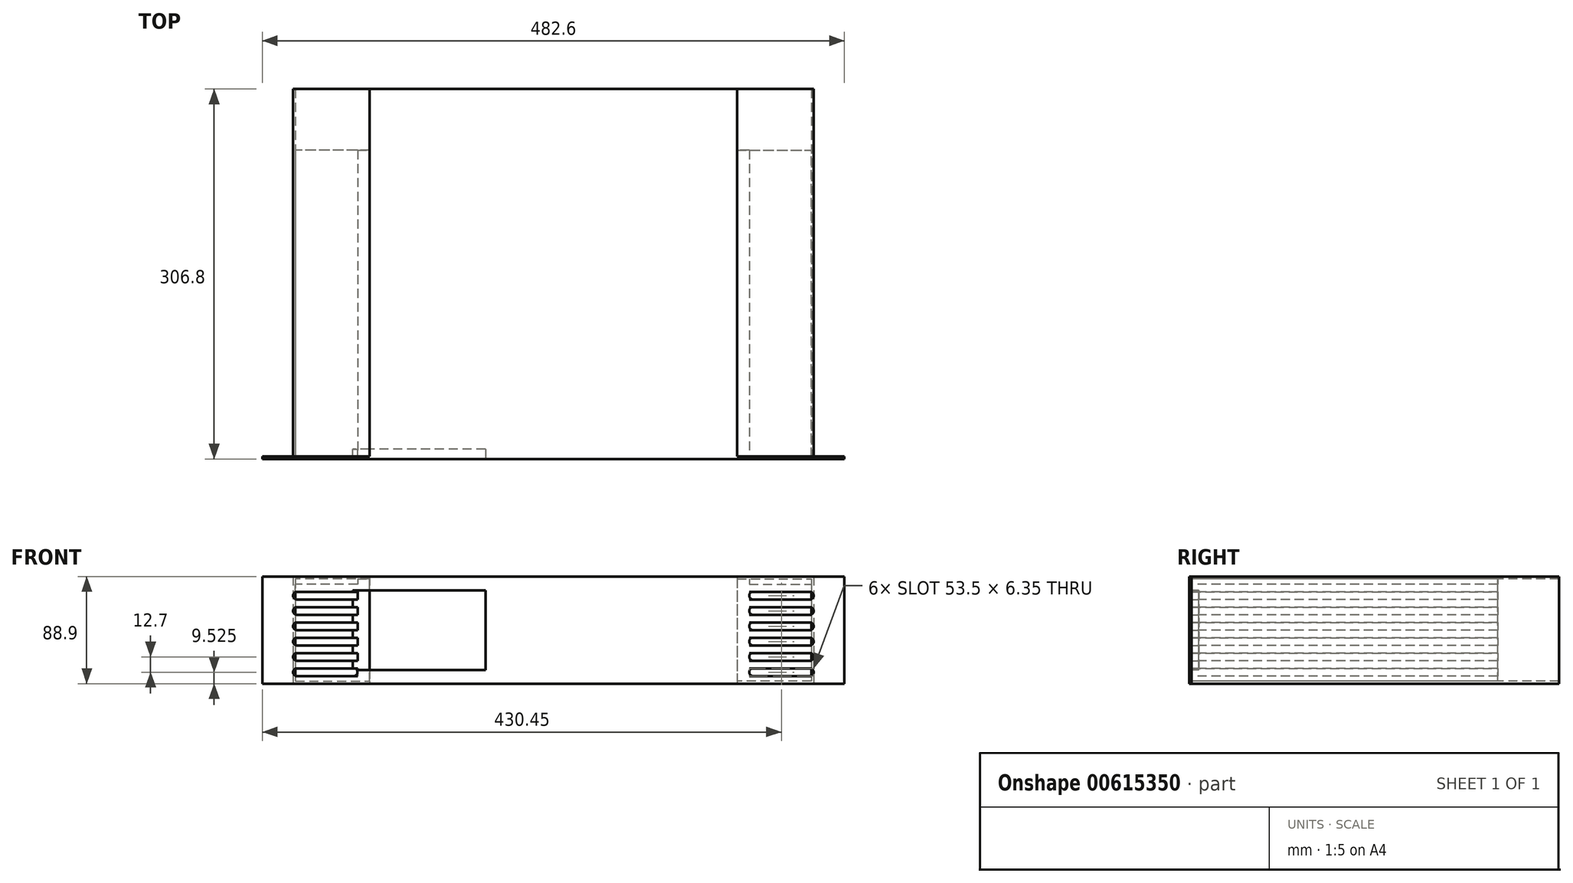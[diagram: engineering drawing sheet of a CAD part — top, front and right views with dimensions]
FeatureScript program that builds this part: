
annotation { "Feature Type Name" : "Feature", "Feature Type Description" : "" }
export const myFeature = defineFeature(function(context is Context, id is Id, definition is map)
    precondition{}
    {
        {
            var Q0;
            Q0=qCreatedBy(makeId("Top.planeOp"),FACE);
            var sketch = newSketch(context, id + "F0", { "sketchPlane" : qUnion([Q0])});
            skLineSegment(sketch, "E0.bottom", {"start": v(152.4, -152.4) * mm, "end": v(-152.4, -152.4) * mm});
            skLineSegment(sketch, "E0.top", {"start": v(152.4, 152.4) * mm, "end": v(-152.4, 152.4) * mm});
            skLineSegment(sketch, "E0.left", {"start": v(152.4, -152.4) * mm, "end": v(152.4, 152.4) * mm});
            skLineSegment(sketch, "E0.right", {"start": v(-152.4, -152.4) * mm, "end": v(-152.4, 152.4) * mm});
            skPoint(sketch, "E0.middle", {"position": v(0, 0) * mm});
            skSolve(sketch);
        }
        {
            var Q0;
            Q0=makeQuery(id+"F0.imprint","IMPRINT",FACE,{"disambiguationData":[TD([[makeQuery(id+"F0.imprint","IMPRINT",EDGE,{"derivedFrom":sQuery(id+"F0.wireOp",EDGE,"E0.bottom")}),-1.0]])]});
            extrude(context, id + "F1", {"entities" : qUnion([Q0]), "depth" : 88.9 * mm, "offsetDistance" : 25 * mm});
        }
        {
            var Q0;
            Q0=makeQuery(id+"F1.opExtrude","SWEPT_FACE",FACE,{"disambiguationData":[OSD([sQuery(id+"F0.wireOp",EDGE,"E0.bottom")])]});
            var sketch = newSketch(context, id + "F2", { "sketchPlane" : qUnion([Q0])});
            skLineSegment(sketch, "E1.bottom", {"start": v(-241.3, 0) * mm, "end": v(241.3, 0) * mm});
            skLineSegment(sketch, "E1.top", {"start": v(-241.3, 88.9) * mm, "end": v(241.3, 88.9) * mm});
            skLineSegment(sketch, "E1.left", {"start": v(-241.3, 0) * mm, "end": v(-241.3, 88.9) * mm});
            skLineSegment(sketch, "E1.right", {"start": v(241.3, 0) * mm, "end": v(241.3, 88.9) * mm});
            skPoint(sketch, "E1.middle", {"position": v(0, 44.45) * mm});
            skPoint(sketch, "E1.middle.positionSnap0", {"position": v(152.4, 44.45) * mm});
            skPoint(sketch, "E1.centerSnap0", {"position": v(152.4, 44.45) * mm});
            skSolve(sketch);
        }
        {
            var Q0;
            {var subQ2=sQuery(id+"F2.wireOp",EDGE,"E1.left");Q0=makeQuery(id+"F2.imprint","IMPRINT",FACE,{"disambiguationData":[TD([[makeQuery(id+"F2.imprint","IMPRINT",EDGE,{"derivedFrom":subQ2}),-1.0]])]});}
            var Q1;
            {var subQ2=sQuery(id+"F2.wireOp",EDGE,"E1.right");Q1=makeQuery(id+"F2.imprint","IMPRINT",FACE,{"disambiguationData":[TD([[makeQuery(id+"F2.imprint","IMPRINT",EDGE,{"derivedFrom":subQ2}),1.0]])]});}
            var Q2;
            {var subQ1=sQuery(id+"F0.wireOp",EDGE,"E0.bottom");var subQ2=makeQuery(id+"F1.opExtrude","SWEPT_EDGE",EDGE,{"disambiguationData":[OSD([subQ1,sQuery(id+"F0.wireOp",EDGE,"E0.left")])]});Q2=makeQuery(id+"F2.imprint","IMPRINT",FACE,{"disambiguationData":[TD([[makeQuery(id+"F2.imprint","IMPRINT",EDGE,{"derivedFrom":subQ2}),-1.0]])]});}
            extrude(context, id + "F3", {"entities" : qUnion([Q0, Q1, Q2]), "operationType" : NewBodyOperationType.ADD, "depth" : 2 * mm, "offsetDistance" : 25 * mm});
        }
        {
            var Q0;
            {var subQ0=sQuery(id+"F2.wireOp",EDGE,"E1.bottom");var subQ2=sQuery(id+"F0.wireOp",EDGE,"E0.left");var subQ5=sQuery(id+"F2.wireOp",EDGE,"E1.top");var subQ6=sQuery(id+"F2.wireOp",EDGE,"E1.right");Q0=makeQuery(id+"F3.boolean.opBoolean","SPLIT",FACE,{"disambiguationData":[TD([makeQuery(id+"F1.opExtrude","SWEPT_FACE",FACE,{"disambiguationData":[OSD([subQ2])]})])],"derivedFrom":makeQuery(id+"F3.opExtrude","CAP_FACE",FACE,{"disambiguationData":[OSD([subQ0,subQ5,sQuery(id+"F2.wireOp",EDGE,"E1.left"),subQ6])],"isStart":true})});}
            var sketch = newSketch(context, id + "F4", { "sketchPlane" : qUnion([Q0])});
            skLineSegment(sketch, "E2", {"start": v(-152.4, 88.9) * mm, "end": v(-162.4, 88.9) * mm});
            skLineSegment(sketch, "E3", {"start": v(-162.4, 88.9) * mm, "end": v(-162.4, 82.55) * mm});
            skLineSegment(sketch, "E4", {"start": v(-162.4, 82.55) * mm, "end": v(-215.9, 82.55) * mm});
            skLineSegment(sketch, "E5", {"start": v(-215.9, 82.55) * mm, "end": v(-215.9, 76.2) * mm});
            skLineSegment(sketch, "E6", {"start": v(-215.9, 76.2) * mm, "end": v(-162.4, 76.2) * mm});
            skLineSegment(sketch, "E7.0.1.1", {"start": v(-215.9, 69.85) * mm, "end": v(-215.9, 63.5) * mm});
            skLineSegment(sketch, "E7.0.1.2", {"start": v(-162.4, 69.85) * mm, "end": v(-215.9, 69.85) * mm});
            skLineSegment(sketch, "E7.0.1.3", {"start": v(-215.9, 63.5) * mm, "end": v(-162.4, 63.5) * mm});
            skLineSegment(sketch, "E7.0.1.4", {"start": v(-162.4, 76.2) * mm, "end": v(-162.4, 69.85) * mm});
            skLineSegment(sketch, "E7.0.2.1", {"start": v(-215.9, 57.15) * mm, "end": v(-215.9, 50.8) * mm});
            skLineSegment(sketch, "E7.0.2.2", {"start": v(-162.4, 57.15) * mm, "end": v(-215.9, 57.15) * mm});
            skLineSegment(sketch, "E7.0.2.3", {"start": v(-215.9, 50.8) * mm, "end": v(-162.4, 50.8) * mm});
            skLineSegment(sketch, "E7.0.2.4", {"start": v(-162.4, 63.5) * mm, "end": v(-162.4, 57.15) * mm});
            skLineSegment(sketch, "E7.0.3.1", {"start": v(-215.9, 44.45) * mm, "end": v(-215.9, 38.1) * mm});
            skLineSegment(sketch, "E7.0.3.2", {"start": v(-162.4, 44.45) * mm, "end": v(-215.9, 44.45) * mm});
            skLineSegment(sketch, "E7.0.3.3", {"start": v(-215.9, 38.1) * mm, "end": v(-162.4, 38.1) * mm});
            skLineSegment(sketch, "E7.0.3.4", {"start": v(-162.4, 50.8) * mm, "end": v(-162.4, 44.45) * mm});
            skLineSegment(sketch, "E7.0.4.1", {"start": v(-215.9, 31.75) * mm, "end": v(-215.9, 25.4) * mm});
            skLineSegment(sketch, "E7.0.4.2", {"start": v(-162.4, 31.75) * mm, "end": v(-215.9, 31.75) * mm});
            skLineSegment(sketch, "E7.0.4.3", {"start": v(-215.9, 25.4) * mm, "end": v(-162.4, 25.4) * mm});
            skLineSegment(sketch, "E7.0.4.4", {"start": v(-162.4, 38.1) * mm, "end": v(-162.4, 31.75) * mm});
            skLineSegment(sketch, "E7.0.5.1", {"start": v(-215.9, 19.05) * mm, "end": v(-215.9, 12.7) * mm});
            skLineSegment(sketch, "E7.0.5.2", {"start": v(-162.4, 19.05) * mm, "end": v(-215.9, 19.05) * mm});
            skLineSegment(sketch, "E7.0.5.3", {"start": v(-215.9, 12.7) * mm, "end": v(-162.4, 12.7) * mm});
            skLineSegment(sketch, "E7.0.5.4", {"start": v(-162.4, 25.4) * mm, "end": v(-162.4, 19.05) * mm});
            skLineSegment(sketch, "E7.0.6.1", {"start": v(-215.9, 6.35) * mm, "end": v(-215.9, 0) * mm});
            skLineSegment(sketch, "E7.0.6.2", {"start": v(-162.4, 6.35) * mm, "end": v(-215.9, 6.35) * mm});
            skLineSegment(sketch, "E7.0.6.3", {"start": v(-215.9, 0) * mm, "end": v(-162.4, 0) * mm});
            skLineSegment(sketch, "E7.0.6.4", {"start": v(-162.4, 12.7) * mm, "end": v(-162.4, 6.35) * mm});
            skLineSegment(sketch, "E7.direction1", {"start": v(-215.9, 76.2) * mm, "end": v(-190.9, 76.2) * mm, "construction": true});
            skLineSegment(sketch, "E7.direction2", {"start": v(-215.9, 76.2) * mm, "end": v(-215.9, 63.5) * mm, "construction": true});
            skLineSegment(sketch, "E8", {"start": v(-162.4, 0) * mm, "end": v(-152.4, 0) * mm});
            skLineSegment(sketch, "E9", {"start": v(-152.4, 0) * mm, "end": v(-152.4, 88.9) * mm});
            skLineSegment(sketch, "E10.MirrorCS", {"start": v(215.9, 69.85) * mm, "end": v(215.9, 63.5) * mm});
            skLineSegment(sketch, "E11.MirrorCS", {"start": v(162.4, 19.05) * mm, "end": v(215.9, 19.05) * mm});
            skLineSegment(sketch, "E12.MirrorCS", {"start": v(162.4, 25.4) * mm, "end": v(162.4, 19.05) * mm});
            skLineSegment(sketch, "E13.MirrorCS", {"start": v(215.9, 57.15) * mm, "end": v(215.9, 50.8) * mm});
            skLineSegment(sketch, "E14.MirrorCS", {"start": v(162.4, 69.85) * mm, "end": v(215.9, 69.85) * mm});
            skLineSegment(sketch, "E15.MirrorCS", {"start": v(215.9, 12.7) * mm, "end": v(162.4, 12.7) * mm});
            skLineSegment(sketch, "E16.MirrorCS", {"start": v(162.4, 88.9) * mm, "end": v(162.4, 82.55) * mm});
            skLineSegment(sketch, "E17.MirrorCS", {"start": v(215.9, 82.55) * mm, "end": v(215.9, 76.2) * mm});
            skLineSegment(sketch, "E18.MirrorCS", {"start": v(152.4, 88.9) * mm, "end": v(162.4, 88.9) * mm});
            skLineSegment(sketch, "E19.MirrorCS", {"start": v(162.4, 82.55) * mm, "end": v(215.9, 82.55) * mm});
            skLineSegment(sketch, "E20.MirrorCS", {"start": v(162.4, 50.8) * mm, "end": v(162.4, 44.45) * mm});
            skLineSegment(sketch, "E21.MirrorCS", {"start": v(215.9, 25.4) * mm, "end": v(162.4, 25.4) * mm});
            skLineSegment(sketch, "E22.MirrorCS", {"start": v(215.9, 44.45) * mm, "end": v(215.9, 38.1) * mm});
            skLineSegment(sketch, "E23.MirrorCS", {"start": v(162.4, 38.1) * mm, "end": v(162.4, 31.75) * mm});
            skLineSegment(sketch, "E24.MirrorCS", {"start": v(162.4, 6.35) * mm, "end": v(215.9, 6.35) * mm});
            skLineSegment(sketch, "E25.MirrorCS", {"start": v(215.9, 6.35) * mm, "end": v(215.9, 0) * mm});
            skLineSegment(sketch, "E26.MirrorCS", {"start": v(215.9, 76.2) * mm, "end": v(215.9, 63.5) * mm, "construction": true});
            skLineSegment(sketch, "E27.MirrorCS", {"start": v(215.9, 76.2) * mm, "end": v(190.9, 76.2) * mm, "construction": true});
            skLineSegment(sketch, "E28.MirrorCS", {"start": v(162.4, 31.75) * mm, "end": v(215.9, 31.75) * mm});
            skLineSegment(sketch, "E29.MirrorCS", {"start": v(152.4, 0) * mm, "end": v(152.4, 88.9) * mm});
            skLineSegment(sketch, "E30.MirrorCS", {"start": v(215.9, 38.1) * mm, "end": v(162.4, 38.1) * mm});
            skLineSegment(sketch, "E31.MirrorCS", {"start": v(162.4, 44.45) * mm, "end": v(215.9, 44.45) * mm});
            skLineSegment(sketch, "E32.MirrorCS", {"start": v(215.9, 76.2) * mm, "end": v(162.4, 76.2) * mm});
            skLineSegment(sketch, "E33.MirrorCS", {"start": v(215.9, 19.05) * mm, "end": v(215.9, 12.7) * mm});
            skLineSegment(sketch, "E34.MirrorCS", {"start": v(215.9, 31.75) * mm, "end": v(215.9, 25.4) * mm});
            skLineSegment(sketch, "E35.MirrorCS", {"start": v(215.9, 63.5) * mm, "end": v(162.4, 63.5) * mm});
            skLineSegment(sketch, "E36.MirrorCS", {"start": v(162.4, 76.2) * mm, "end": v(162.4, 69.85) * mm});
            skLineSegment(sketch, "E37.MirrorCS", {"start": v(215.9, 50.8) * mm, "end": v(162.4, 50.8) * mm});
            skLineSegment(sketch, "E38.MirrorCS", {"start": v(162.4, 57.15) * mm, "end": v(215.9, 57.15) * mm});
            skLineSegment(sketch, "E39.MirrorCS", {"start": v(162.4, 12.7) * mm, "end": v(162.4, 6.35) * mm});
            skLineSegment(sketch, "E40.MirrorCS", {"start": v(162.4, 63.5) * mm, "end": v(162.4, 57.15) * mm});
            skLineSegment(sketch, "E41.MirrorCS", {"start": v(215.9, 0) * mm, "end": v(162.4, 0) * mm});
            skLineSegment(sketch, "E42.MirrorCS", {"start": v(162.4, 0) * mm, "end": v(152.4, 0) * mm});
            skSolve(sketch);
        }
        {
            var Q0;
            Q0=makeQuery(id+"F4.imprint","IMPRINT",FACE,{"disambiguationData":[TD([[makeQuery(id+"F4.imprint","IMPRINT",EDGE,{"derivedFrom":sQuery(id+"F4.wireOp",EDGE,"E2")}),1.0]])]});
            var Q1;
            Q1=makeQuery(id+"F4.imprint","IMPRINT",FACE,{"disambiguationData":[TD([[makeQuery(id+"F4.imprint","IMPRINT",EDGE,{"derivedFrom":sQuery(id+"F4.wireOp",EDGE,"E10.MirrorCS")}),-1.0]])]});
            extrude(context, id + "F5", {"entities" : qUnion([Q0, Q1]), "depth" : 254 * mm, "offsetDistance" : 25 * mm});
        }
        {
            var Q0;
            {var subQ0=sQuery(id+"F2.wireOp",EDGE,"E1.bottom");var subQ2=sQuery(id+"F0.wireOp",EDGE,"E0.left");var subQ5=sQuery(id+"F2.wireOp",EDGE,"E1.top");var subQ6=sQuery(id+"F2.wireOp",EDGE,"E1.right");Q0=makeQuery(id+"F3.boolean.opBoolean","SPLIT",FACE,{"disambiguationData":[TD([makeQuery(id+"F1.opExtrude","SWEPT_FACE",FACE,{"disambiguationData":[OSD([subQ2])]})])],"derivedFrom":makeQuery(id+"F3.opExtrude","CAP_FACE",FACE,{"disambiguationData":[OSD([subQ0,subQ5,sQuery(id+"F2.wireOp",EDGE,"E1.left"),subQ6])],"isStart":true})});}
            var sketch = newSketch(context, id + "F6", { "sketchPlane" : qUnion([Q0])});
            skArc(sketch, "E43", {"start": v(-212.72, 76.2) * mm, "mid": v(-215.9, 73.03) * mm, "end": v(-212.72, 69.85) * mm});
            skArc(sketch, "E44", {"start": v(-165.57, 69.85) * mm, "mid": v(-162.4, 73.03) * mm, "end": v(-165.57, 76.2) * mm});
            skLineSegment(sketch, "E45", {"start": v(-212.72, 69.85) * mm, "end": v(-165.57, 69.85) * mm});
            skLineSegment(sketch, "E46", {"start": v(-212.72, 76.2) * mm, "end": v(-165.57, 76.2) * mm});
            skArc(sketch, "E47.0.1.0", {"start": v(-212.72, 63.5) * mm, "mid": v(-215.9, 60.33) * mm, "end": v(-212.72, 57.15) * mm});
            skLineSegment(sketch, "E47.0.1.1", {"start": v(-212.72, 57.15) * mm, "end": v(-165.57, 57.15) * mm});
            skLineSegment(sketch, "E47.0.1.2", {"start": v(-212.72, 63.5) * mm, "end": v(-165.57, 63.5) * mm});
            skArc(sketch, "E47.0.1.3", {"start": v(-165.57, 57.15) * mm, "mid": v(-162.4, 60.33) * mm, "end": v(-165.57, 63.5) * mm});
            skArc(sketch, "E47.0.2.0", {"start": v(-212.72, 50.8) * mm, "mid": v(-215.9, 47.62) * mm, "end": v(-212.72, 44.45) * mm});
            skLineSegment(sketch, "E47.0.2.1", {"start": v(-212.72, 44.45) * mm, "end": v(-165.57, 44.45) * mm});
            skLineSegment(sketch, "E47.0.2.2", {"start": v(-212.72, 50.8) * mm, "end": v(-165.57, 50.8) * mm});
            skArc(sketch, "E47.0.2.3", {"start": v(-165.57, 44.45) * mm, "mid": v(-162.4, 47.62) * mm, "end": v(-165.57, 50.8) * mm});
            skArc(sketch, "E47.0.3.0", {"start": v(-212.72, 38.1) * mm, "mid": v(-215.9, 34.92) * mm, "end": v(-212.72, 31.75) * mm});
            skLineSegment(sketch, "E47.0.3.1", {"start": v(-212.72, 31.75) * mm, "end": v(-165.57, 31.75) * mm});
            skLineSegment(sketch, "E47.0.3.2", {"start": v(-212.72, 38.1) * mm, "end": v(-165.57, 38.1) * mm});
            skArc(sketch, "E47.0.3.3", {"start": v(-165.57, 31.75) * mm, "mid": v(-162.4, 34.92) * mm, "end": v(-165.57, 38.1) * mm});
            skArc(sketch, "E47.0.4.0", {"start": v(-212.72, 25.4) * mm, "mid": v(-215.9, 22.22) * mm, "end": v(-212.72, 19.05) * mm});
            skLineSegment(sketch, "E47.0.4.1", {"start": v(-212.72, 19.05) * mm, "end": v(-165.57, 19.05) * mm});
            skLineSegment(sketch, "E47.0.4.2", {"start": v(-212.72, 25.4) * mm, "end": v(-165.57, 25.4) * mm});
            skArc(sketch, "E47.0.4.3", {"start": v(-165.57, 19.05) * mm, "mid": v(-162.4, 22.22) * mm, "end": v(-165.57, 25.4) * mm});
            skArc(sketch, "E47.0.5.0", {"start": v(-212.72, 12.7) * mm, "mid": v(-215.9, 9.52) * mm, "end": v(-212.72, 6.35) * mm});
            skLineSegment(sketch, "E47.0.5.1", {"start": v(-212.72, 6.35) * mm, "end": v(-165.57, 6.35) * mm});
            skLineSegment(sketch, "E47.0.5.2", {"start": v(-212.72, 12.7) * mm, "end": v(-165.57, 12.7) * mm});
            skArc(sketch, "E47.0.5.3", {"start": v(-165.57, 6.35) * mm, "mid": v(-162.4, 9.52) * mm, "end": v(-165.57, 12.7) * mm});
            skLineSegment(sketch, "E47.direction1", {"start": v(-212.72, 69.85) * mm, "end": v(-187.72, 69.85) * mm, "construction": true});
            skLineSegment(sketch, "E47.direction2", {"start": v(-212.72, 69.85) * mm, "end": v(-212.72, 57.15) * mm, "construction": true});
            skArc(sketch, "E48.MirrorCS", {"start": v(212.72, 38.1) * mm, "mid": v(215.9, 34.92) * mm, "end": v(212.72, 31.75) * mm});
            skLineSegment(sketch, "E49.MirrorCS", {"start": v(212.72, 6.35) * mm, "end": v(165.57, 6.35) * mm});
            skArc(sketch, "E50.MirrorCS", {"start": v(165.57, 44.45) * mm, "mid": v(162.4, 47.62) * mm, "end": v(165.57, 50.8) * mm});
            skLineSegment(sketch, "E51.MirrorCS", {"start": v(212.72, 50.8) * mm, "end": v(165.57, 50.8) * mm});
            skLineSegment(sketch, "E52.MirrorCS", {"start": v(212.72, 44.45) * mm, "end": v(165.57, 44.45) * mm});
            skArc(sketch, "E53.MirrorCS", {"start": v(212.72, 50.8) * mm, "mid": v(215.9, 47.62) * mm, "end": v(212.72, 44.45) * mm});
            skArc(sketch, "E54.MirrorCS", {"start": v(165.57, 57.15) * mm, "mid": v(162.4, 60.33) * mm, "end": v(165.57, 63.5) * mm});
            skLineSegment(sketch, "E55.MirrorCS", {"start": v(212.72, 69.85) * mm, "end": v(212.72, 57.15) * mm, "construction": true});
            skLineSegment(sketch, "E56.MirrorCS", {"start": v(212.72, 69.85) * mm, "end": v(187.72, 69.85) * mm, "construction": true});
            skLineSegment(sketch, "E57.MirrorCS", {"start": v(212.72, 63.5) * mm, "end": v(165.57, 63.5) * mm});
            skLineSegment(sketch, "E58.MirrorCS", {"start": v(212.72, 57.15) * mm, "end": v(165.57, 57.15) * mm});
            skArc(sketch, "E59.MirrorCS", {"start": v(212.72, 63.5) * mm, "mid": v(215.9, 60.33) * mm, "end": v(212.72, 57.15) * mm});
            skLineSegment(sketch, "E60.MirrorCS", {"start": v(212.72, 76.2) * mm, "end": v(165.57, 76.2) * mm});
            skLineSegment(sketch, "E61.MirrorCS", {"start": v(212.72, 69.85) * mm, "end": v(165.57, 69.85) * mm});
            skLineSegment(sketch, "E62.MirrorCS", {"start": v(212.72, 19.05) * mm, "end": v(165.57, 19.05) * mm});
            skArc(sketch, "E63.MirrorCS", {"start": v(165.57, 69.85) * mm, "mid": v(162.4, 73.03) * mm, "end": v(165.57, 76.2) * mm});
            skArc(sketch, "E64.MirrorCS", {"start": v(212.72, 76.2) * mm, "mid": v(215.9, 73.03) * mm, "end": v(212.72, 69.85) * mm});
            skArc(sketch, "E65.MirrorCS", {"start": v(165.57, 31.75) * mm, "mid": v(162.4, 34.92) * mm, "end": v(165.57, 38.1) * mm});
            skArc(sketch, "E66.MirrorCS", {"start": v(212.72, 25.4) * mm, "mid": v(215.9, 22.22) * mm, "end": v(212.72, 19.05) * mm});
            skLineSegment(sketch, "E67.MirrorCS", {"start": v(212.72, 31.75) * mm, "end": v(165.57, 31.75) * mm});
            skArc(sketch, "E68.MirrorCS", {"start": v(165.57, 19.05) * mm, "mid": v(162.4, 22.22) * mm, "end": v(165.57, 25.4) * mm});
            skLineSegment(sketch, "E69.MirrorCS", {"start": v(212.72, 38.1) * mm, "end": v(165.57, 38.1) * mm});
            skArc(sketch, "E70.MirrorCS", {"start": v(165.57, 6.35) * mm, "mid": v(162.4, 9.52) * mm, "end": v(165.57, 12.7) * mm});
            skLineSegment(sketch, "E71.MirrorCS", {"start": v(212.72, 25.4) * mm, "end": v(165.57, 25.4) * mm});
            skLineSegment(sketch, "E72.MirrorCS", {"start": v(212.72, 12.7) * mm, "end": v(165.57, 12.7) * mm});
            skArc(sketch, "E73.MirrorCS", {"start": v(212.72, 12.7) * mm, "mid": v(215.9, 9.52) * mm, "end": v(212.72, 6.35) * mm});
            skSolve(sketch);
        }
        {
            var Q0;
            Q0 = qSketchRegion(id + "F6", true);
            extrude(context, id + "F7", {"entities" : qUnion([Q0]), "operationType" : NewBodyOperationType.REMOVE, "endBound" : BoundingType.THROUGH_ALL, "oppositeDirection" : true, "depth" : 25 * mm, "offsetDistance" : 25 * mm});
        }
        {
            var Q0;
            {var subQ0=sQuery(id+"F2.wireOp",EDGE,"E1.bottom");var subQ2=sQuery(id+"F0.wireOp",EDGE,"E0.left");var subQ5=sQuery(id+"F2.wireOp",EDGE,"E1.top");var subQ6=sQuery(id+"F2.wireOp",EDGE,"E1.right");Q0=makeQuery(id+"F3.boolean.opBoolean","SPLIT",FACE,{"disambiguationData":[TD([makeQuery(id+"F1.opExtrude","SWEPT_FACE",FACE,{"disambiguationData":[OSD([subQ2])]})])],"derivedFrom":makeQuery(id+"F3.opExtrude","CAP_FACE",FACE,{"disambiguationData":[OSD([subQ0,subQ5,sQuery(id+"F2.wireOp",EDGE,"E1.left"),subQ6])],"isStart":true})});}
            var sketch = newSketch(context, id + "F8", { "sketchPlane" : qUnion([Q0])});
            skLineSegment(sketch, "E74", {"start": v(-152.4, 88.9) * mm, "end": v(-215.9, 88.9) * mm});
            skLineSegment(sketch, "E75", {"start": v(-215.9, 88.9) * mm, "end": v(-215.9, 0) * mm});
            skLineSegment(sketch, "E76", {"start": v(-215.9, 0) * mm, "end": v(-152.4, 0) * mm});
            skLineSegment(sketch, "E77", {"start": v(-152.4, 88.9) * mm, "end": v(-152.4, 86.9) * mm});
            skLineSegment(sketch, "E78", {"start": v(-152.4, 86.9) * mm, "end": v(-213.9, 86.9) * mm});
            skLineSegment(sketch, "E79", {"start": v(-213.9, 86.9) * mm, "end": v(-213.9, 2) * mm});
            skLineSegment(sketch, "E80", {"start": v(-213.9, 2) * mm, "end": v(-152.4, 2) * mm});
            skLineSegment(sketch, "E81", {"start": v(-152.4, 2) * mm, "end": v(-152.4, 0) * mm});
            skLineSegment(sketch, "E82.MirrorCS", {"start": v(152.4, 88.9) * mm, "end": v(152.4, 86.9) * mm});
            skLineSegment(sketch, "E83.MirrorCS", {"start": v(152.4, 2) * mm, "end": v(152.4, 0) * mm});
            skLineSegment(sketch, "E84.MirrorCS", {"start": v(215.9, 88.9) * mm, "end": v(215.9, 0) * mm});
            skLineSegment(sketch, "E85.MirrorCS", {"start": v(215.9, 0) * mm, "end": v(152.4, 0) * mm});
            skLineSegment(sketch, "E86.MirrorCS", {"start": v(152.4, 86.9) * mm, "end": v(213.9, 86.9) * mm});
            skLineSegment(sketch, "E87.MirrorCS", {"start": v(213.9, 2) * mm, "end": v(152.4, 2) * mm});
            skLineSegment(sketch, "E88.MirrorCS", {"start": v(152.4, 88.9) * mm, "end": v(215.9, 88.9) * mm});
            skLineSegment(sketch, "E89.MirrorCS", {"start": v(213.9, 86.9) * mm, "end": v(213.9, 2) * mm});
            skSolve(sketch);
        }
        {
            var Q0;
            Q0 = qSketchRegion(id + "F8", true);
            extrude(context, id + "F9", {"entities" : qUnion([Q0]), "operationType" : NewBodyOperationType.REMOVE, "endBound" : BoundingType.THROUGH_ALL, "depth" : 25 * mm, "offsetDistance" : 25 * mm});
        }
        {
            var Q0;
            Q0 = qSketchRegion(id + "F8", true);
            extrude(context, id + "F10", {"entities" : qUnion([Q0]), "depth" : 304.8 * mm, "offsetDistance" : 25 * mm});
        }
        {
            var Q0;
            Q0=makeQuery(id+"F3.opExtrude","CAP_FACE",FACE,{"disambiguationData":[OSD([sQuery(id+"F2.wireOp",EDGE,"E1.bottom"),sQuery(id+"F2.wireOp",EDGE,"E1.top"),sQuery(id+"F2.wireOp",EDGE,"E1.left"),sQuery(id+"F2.wireOp",EDGE,"E1.right")])],"isStart":false});
            var sketch = newSketch(context, id + "F11", { "sketchPlane" : qUnion([Q0])});
            skLineSegment(sketch, "E90.bottom", {"start": v(-56.3, 11.45) * mm, "end": v(-166.3, 11.45) * mm});
            skLineSegment(sketch, "E90.top", {"start": v(-56.3, 77.45) * mm, "end": v(-166.3, 77.45) * mm});
            skLineSegment(sketch, "E90.left", {"start": v(-56.3, 11.45) * mm, "end": v(-56.3, 77.45) * mm});
            skLineSegment(sketch, "E90.right", {"start": v(-166.3, 11.45) * mm, "end": v(-166.3, 77.45) * mm});
            skPoint(sketch, "E90.middle", {"position": v(-111.3, 44.45) * mm});
            skSolve(sketch);
        }
        {
            var Q0;
            Q0 = qSketchRegion(id + "F11", true);
            extrude(context, id + "F12", {"entities" : qUnion([Q0]), "operationType" : NewBodyOperationType.REMOVE, "oppositeDirection" : true, "depth" : 8 * mm, "offsetDistance" : 25 * mm});
        }
    });
